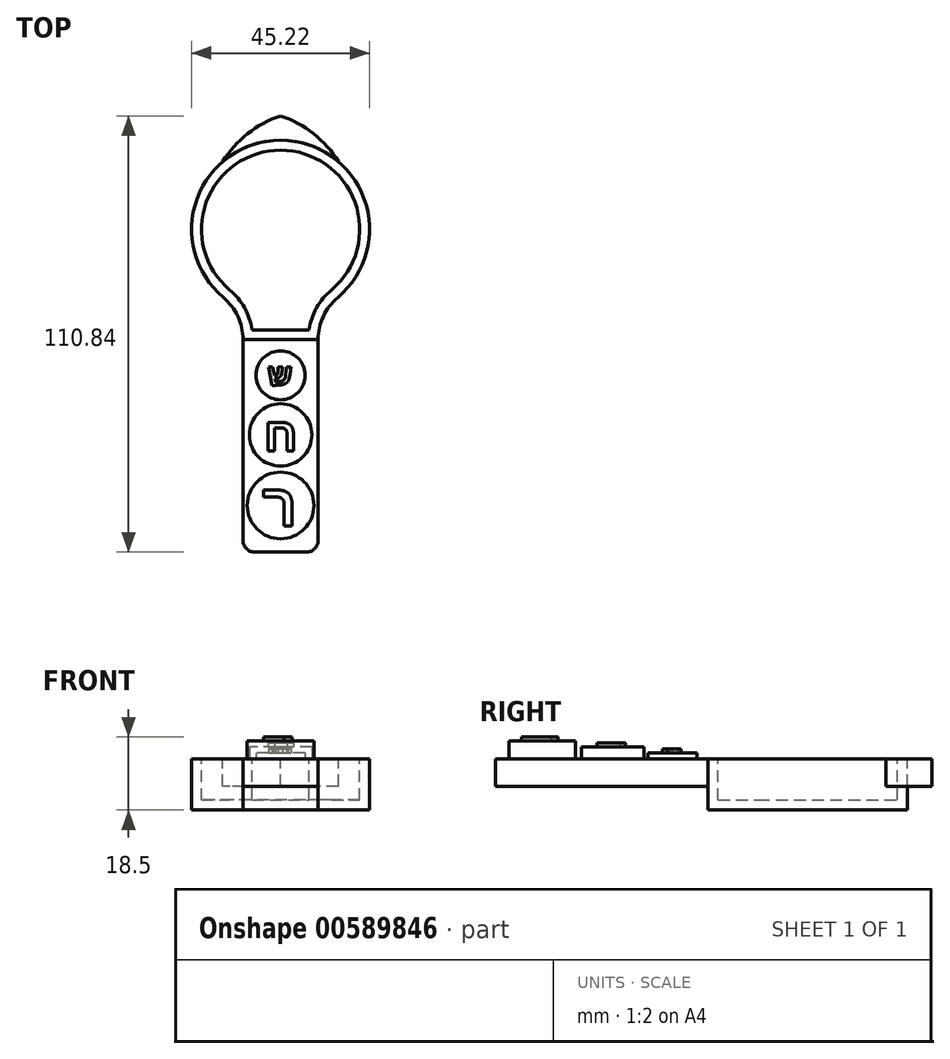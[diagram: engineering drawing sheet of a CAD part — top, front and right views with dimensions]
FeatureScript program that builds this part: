
annotation { "Feature Type Name" : "Feature", "Feature Type Description" : "" }
export const myFeature = defineFeature(function(context is Context, id is Id, definition is map)
    precondition{}
    {
        {
            var Q0;
            Q0=qCreatedBy(makeId("Top.planeOp"),FACE);
            var sketch = newSketch(context, id + "F0", { "sketchPlane" : qUnion([Q0])});
            skLineSegment(sketch, "E0", {"start": v(2, -64.73) * mm, "end": v(6.54, -64.73) * mm});
            skLineSegment(sketch, "E1", {"start": v(9.54, -61.73) * mm, "end": v(9.54, -10.73) * mm});
            skArc(sketch, "E2", {"start": v(14.54, 0) * mm, "mid": v(21.24, 25.05) * mm, "end": v(0, 39.91) * mm});
            skPoint(sketch, "E2.centerSnap0", {"position": v(0, 0) * mm});
            skArc(sketch, "E3", {"start": v(14.54, 0) * mm, "mid": v(10.85, -4.81) * mm, "end": v(9.54, -10.73) * mm});
            skPoint(sketch, "E4.orphan", {"position": v(9.54, 0) * mm});
            skArc(sketch, "E5.MirrorCS", {"start": v(-14.54, 0) * mm, "mid": v(-21.24, 25.05) * mm, "end": v(0, 39.91) * mm});
            skArc(sketch, "E6.MirrorCS", {"start": v(-14.54, 0) * mm, "mid": v(-10.85, -4.81) * mm, "end": v(-9.54, -10.73) * mm});
            skLineSegment(sketch, "E7.MirrorCS", {"start": v(-9.54, -61.73) * mm, "end": v(-9.54, -10.73) * mm});
            skPoint(sketch, "E8.visualSharp", {"position": v(9.54, -64.73) * mm});
            skArc(sketch, "E8.filletArc", {"start": v(6.54, -64.73) * mm, "mid": v(8.66, -63.85) * mm, "end": v(9.54, -61.73) * mm});
            skLineSegment(sketch, "E9.MirrorCS", {"start": v(-2, -64.73) * mm, "end": v(-6.54, -64.73) * mm});
            skArc(sketch, "E10.MirrorCS", {"start": v(-6.54, -64.73) * mm, "mid": v(-8.66, -63.85) * mm, "end": v(-9.54, -61.73) * mm});
            skLineSegment(sketch, "E11", {"start": v(-2, -64.73) * mm, "end": v(2, -64.73) * mm});
            skArc(sketch, "E12", {"start": v(0, 46.1) * mm, "mid": v(-8.38, 41.56) * mm, "end": v(-14.73, 34.46) * mm});
            skArc(sketch, "E13.MirrorCS", {"start": v(0, 46.1) * mm, "mid": v(8.38, 41.56) * mm, "end": v(14.73, 34.46) * mm});
            skLineSegment(sketch, "E14", {"start": v(-9.54, -10.73) * mm, "end": v(9.54, -10.73) * mm});
            skSolve(sketch);
        }
        {
            var Q0;
            {var subQ4=sQuery(id+"F0.wireOp",EDGE,"E12");Q0=makeQuery(id+"F0.imprint","IMPRINT",FACE,{"disambiguationData":[TD([[makeQuery(id+"F0.imprint","IMPRINT",EDGE,{"derivedFrom":subQ4}),1.0]])]});}
            extrude(context, id + "F1", {"entities" : qUnion([Q0]), "oppositeDirection" : true, "depth" : 7 * mm, "offsetDistance" : 25 * mm});
        }
        {
            var Q0;
            {var subQ3=sQuery(id+"F0.wireOp",EDGE,"E3");Q0=makeQuery(id+"F0.imprint","IMPRINT",FACE,{"disambiguationData":[TD([[makeQuery(id+"F0.imprint","IMPRINT",EDGE,{"derivedFrom":subQ3}),-1.0]])]});}
            extrude(context, id + "F2", {"entities" : qUnion([Q0]), "oppositeDirection" : true, "depth" : 13 * mm, "offsetDistance" : 25 * mm});
        }
        {
            var Q0;
            Q0=makeQuery(id+"F0.imprint","IMPRINT",FACE,{"disambiguationData":[TD([[makeQuery(id+"F0.imprint","IMPRINT",EDGE,{"derivedFrom":sQuery(id+"F0.wireOp",EDGE,"E0")}),1.0]])]});
            extrude(context, id + "F3", {"entities" : qUnion([Q0]), "oppositeDirection" : true, "depth" : 7 * mm, "offsetDistance" : 25 * mm});
        }
        {
            var Q0;
            Q0=makeQuery(id+"F2.opExtrude","CAP_FACE",FACE,{"disambiguationData":[OSD([sQuery(id+"F0.wireOp",EDGE,"E2"),sQuery(id+"F0.wireOp",EDGE,"E3"),sQuery(id+"F0.wireOp",EDGE,"E5.MirrorCS"),sQuery(id+"F0.wireOp",EDGE,"E6.MirrorCS"),sQuery(id+"F0.wireOp",EDGE,"E14")])],"isStart":true});
            shell(context, id + "F4", {"entities" : qUnion([Q0]), "thickness" : 2.5 * mm});
        }
        {
            var Q0;
            Q0=makeQuery(id+"F3.opExtrude","CAP_FACE",FACE,{"disambiguationData":[OSD([sQuery(id+"F0.wireOp",EDGE,"E0"),sQuery(id+"F0.wireOp",EDGE,"E1"),sQuery(id+"F0.wireOp",EDGE,"E7.MirrorCS"),sQuery(id+"F0.wireOp",EDGE,"E8.filletArc"),sQuery(id+"F0.wireOp",EDGE,"E9.MirrorCS"),sQuery(id+"F0.wireOp",EDGE,"E10.MirrorCS"),sQuery(id+"F0.wireOp",EDGE,"E11"),sQuery(id+"F0.wireOp",EDGE,"E14")])],"isStart":true});
            var sketch = newSketch(context, id + "F5", { "sketchPlane" : qUnion([Q0])});
            skCircle(sketch, "E15", {"center": v(0, -19.8) * mm, "radius": 6.22 * mm});
            skCircle(sketch, "E16", {"center": v(0, -34.93) * mm, "radius": 7.93 * mm});
            skCircle(sketch, "E17", {"center": v(0, -52.86) * mm, "radius": 8.47 * mm});
            skSolve(sketch);
        }
        {
            var Q0;
            Q0=makeQuery(id+"F5.imprint","IMPRINT",FACE,{"disambiguationData":[TD([[makeQuery(id+"F5.imprint","IMPRINT",EDGE,{"derivedFrom":sQuery(id+"F5.wireOp",EDGE,"E15")}),1.0]])]});
            extrude(context, id + "F6", {"entities" : qUnion([Q0]), "operationType" : NewBodyOperationType.ADD, "depth" : 1.5 * mm, "offsetDistance" : 25 * mm});
        }
        {
            var Q0;
            Q0=makeQuery(id+"F5.imprint","IMPRINT",FACE,{"disambiguationData":[TD([[makeQuery(id+"F5.imprint","IMPRINT",EDGE,{"derivedFrom":sQuery(id+"F5.wireOp",EDGE,"E16")}),1.0]])]});
            extrude(context, id + "F7", {"entities" : qUnion([Q0]), "operationType" : NewBodyOperationType.ADD, "depth" : 3 * mm, "offsetDistance" : 25 * mm});
        }
        {
            var Q0;
            Q0=makeQuery(id+"F5.imprint","IMPRINT",FACE,{"disambiguationData":[TD([[makeQuery(id+"F5.imprint","IMPRINT",EDGE,{"derivedFrom":sQuery(id+"F5.wireOp",EDGE,"E17")}),1.0]])]});
            extrude(context, id + "F8", {"entities" : qUnion([Q0]), "operationType" : NewBodyOperationType.ADD, "depth" : 4.5 * mm, "offsetDistance" : 25 * mm});
        }
        {
            var Q0;
            Q0=makeQuery(id+"F6.opExtrude","CAP_FACE",FACE,{"disambiguationData":[OSD([sQuery(id+"F5.wireOp",EDGE,"E15")])],"isStart":false});
            var sketch = newSketch(context, id + "F9", { "sketchPlane" : qUnion([Q0])});
            skText(sketch, "E18", { "text": "ש", "fontName": "Arimo-Bold.ttf"});
            const initialGuessF9  = {"E18": [-0.00326, -0.0223, 1, 0, 0.0055]};
            skSetInitialGuess(sketch, initialGuessF9);
            skSolve(sketch);
        }
        {
            var Q0;
            Q0 = qSketchRegion(id + "F9", true);
            extrude(context, id + "F10", {"entities" : qUnion([Q0]), "operationType" : NewBodyOperationType.ADD, "depth" : 1 * mm, "offsetDistance" : 25 * mm});
        }
        {
            var Q0;
            Q0=makeQuery(id+"F7.opExtrude","CAP_FACE",FACE,{"disambiguationData":[OSD([sQuery(id+"F5.wireOp",EDGE,"E16")])],"isStart":false});
            var sketch = newSketch(context, id + "F11", { "sketchPlane" : qUnion([Q0])});
            skText(sketch, "E19", { "text": "ח", "fontName": "Arimo-Bold.ttf"});
            const initialGuessF11  = {"E19": [-0.00419, -0.03902, 1, 0, 0.00866]};
            skSetInitialGuess(sketch, initialGuessF11);
            skSolve(sketch);
        }
        {
            var Q0;
            Q0 = qSketchRegion(id + "F11", true);
            extrude(context, id + "F12", {"entities" : qUnion([Q0]), "operationType" : NewBodyOperationType.ADD, "depth" : 1 * mm, "offsetDistance" : 25 * mm});
        }
        {
            var Q0;
            Q0=makeQuery(id+"F8.opExtrude","CAP_FACE",FACE,{"disambiguationData":[OSD([sQuery(id+"F5.wireOp",EDGE,"E17")])],"isStart":false});
            var sketch = newSketch(context, id + "F13", { "sketchPlane" : qUnion([Q0])});
            skText(sketch, "E20", { "text": "ר", "fontName": "Arimo-Bold.ttf"});
            const initialGuessF13  = {"E20": [-0.00462, -0.05812, 1, 0, 0.01094]};
            skSetInitialGuess(sketch, initialGuessF13);
            skSolve(sketch);
        }
        {
            var Q0;
            Q0 = qSketchRegion(id + "F13", true);
            extrude(context, id + "F14", {"entities" : qUnion([Q0]), "operationType" : NewBodyOperationType.ADD, "depth" : 1 * mm, "offsetDistance" : 25 * mm});
        }
    });
